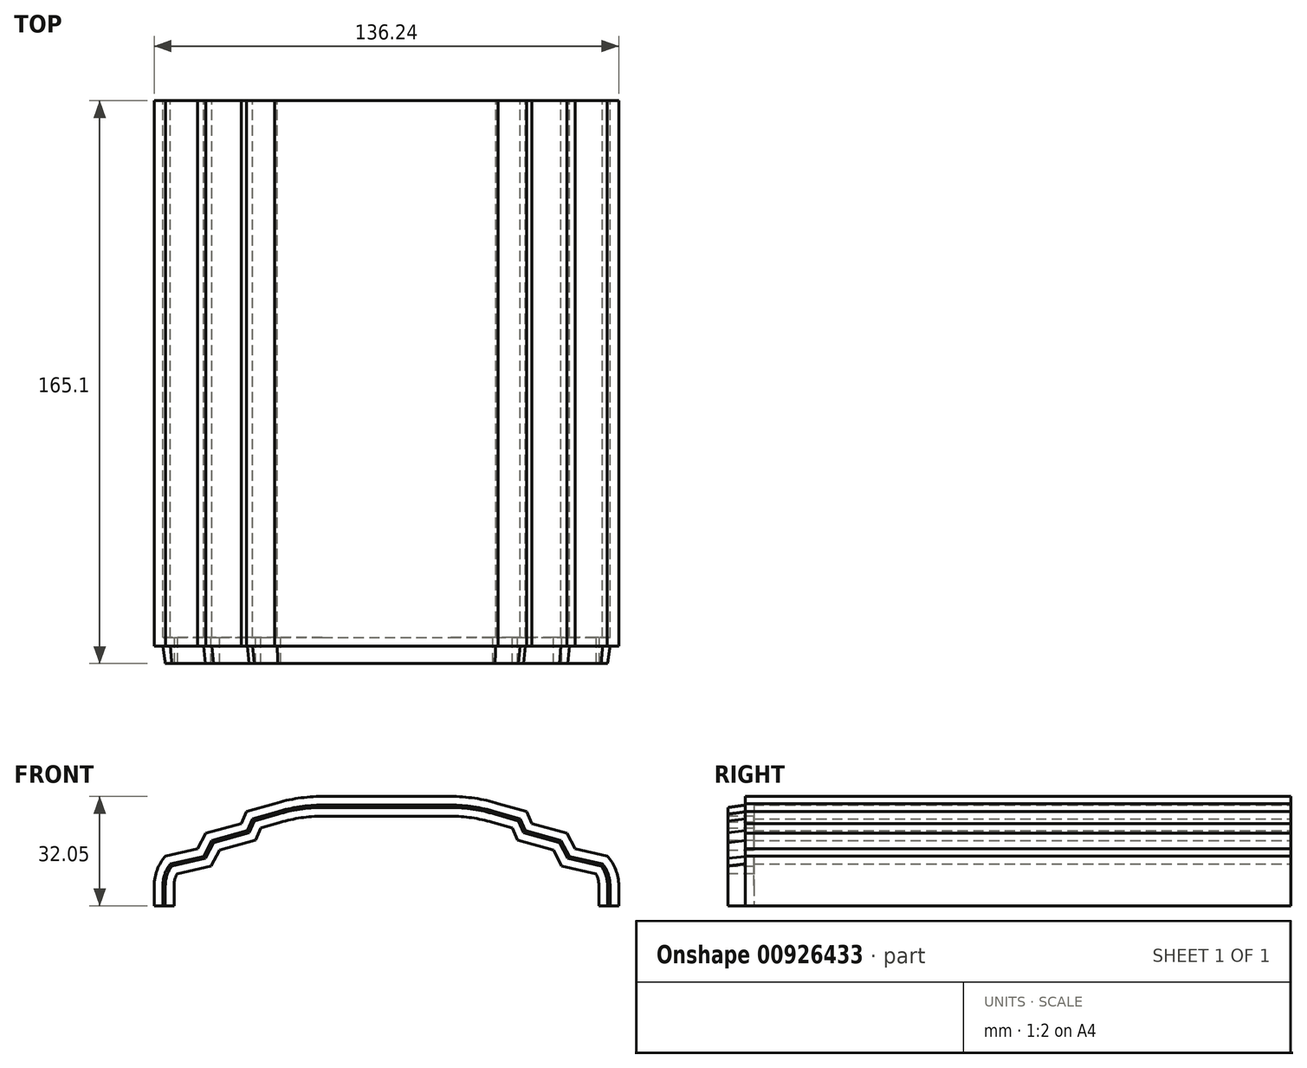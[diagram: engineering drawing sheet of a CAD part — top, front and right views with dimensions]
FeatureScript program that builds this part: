
annotation { "Feature Type Name" : "Feature", "Feature Type Description" : "" }
export const myFeature = defineFeature(function(context is Context, id is Id, definition is map)
    precondition{}
    {
        {
            var Q0;
            Q0=qCreatedBy(makeId("Front.planeOp"),FACE);
            var sketch = newSketch(context, id + "F0", { "sketchPlane" : qUnion([Q0])});
            skLineSegment(sketch, "E0", {"start": v(65.58, 0) * mm, "end": v(68.12, 0) * mm});
            skLineSegment(sketch, "E1", {"start": v(68.12, 0) * mm, "end": v(68.12, 5.92) * mm});
            skArc(sketch, "E2", {"start": v(68.12, 5.92) * mm, "mid": v(67.26, 10.55) * mm, "end": v(64.79, 14.56) * mm});
            skLineSegment(sketch, "E3", {"start": v(64.79, 14.56) * mm, "end": v(55.34, 16.7) * mm});
            skLineSegment(sketch, "E4", {"start": v(55.34, 16.7) * mm, "end": v(52.95, 21.32) * mm});
            skLineSegment(sketch, "E5", {"start": v(52.95, 21.32) * mm, "end": v(42.61, 24.13) * mm});
            skLineSegment(sketch, "E6", {"start": v(42.61, 24.13) * mm, "end": v(41.07, 27.59) * mm});
            skLineSegment(sketch, "E7", {"start": v(41.07, 27.59) * mm, "end": v(32.77, 29.98) * mm});
            skArc(sketch, "E8", {"start": v(32.77, 29.98) * mm, "mid": v(25.87, 31.53) * mm, "end": v(18.83, 32.05) * mm});
            skLineSegment(sketch, "E9", {"start": v(18.83, 32.05) * mm, "end": v(0, 32.05) * mm});
            skLineSegment(sketch, "E10", {"start": v(0, 32.05) * mm, "end": v(0, 29.5) * mm});
            skLineSegment(sketch, "E11.0", {"start": v(18.83, 29.5) * mm, "end": v(0, 29.5) * mm});
            skArc(sketch, "E11.1", {"start": v(32.05, 27.55) * mm, "mid": v(25.51, 29.02) * mm, "end": v(18.83, 29.5) * mm});
            skLineSegment(sketch, "E11.2", {"start": v(39.23, 25.47) * mm, "end": v(32.05, 27.55) * mm});
            skLineSegment(sketch, "E11.3", {"start": v(40.78, 22) * mm, "end": v(39.23, 25.47) * mm});
            skLineSegment(sketch, "E11.4", {"start": v(51.2, 19.16) * mm, "end": v(40.78, 22) * mm});
            skLineSegment(sketch, "E11.5", {"start": v(65.58, 0) * mm, "end": v(65.58, 5.92) * mm});
            skArc(sketch, "E11.6", {"start": v(65.58, 5.92) * mm, "mid": v(65.02, 9.28) * mm, "end": v(63.4, 12.28) * mm});
            skLineSegment(sketch, "E11.7", {"start": v(63.4, 12.28) * mm, "end": v(53.63, 14.49) * mm});
            skLineSegment(sketch, "E11.8", {"start": v(53.63, 14.49) * mm, "end": v(51.2, 19.16) * mm});
            skSolve(sketch);
        }
        {
            var Q0;
            Q0 = qSketchRegion(id + "F0", true);
            extrude(context, id + "F1", {"entities" : qUnion([Q0]), "depth" : 160.02 * mm, "offsetDistance" : 25.4 * mm});
        }
        {
            var Q0;
            Q0=makeQuery(id+"F1.opExtrude","SWEPT_FACE",FACE,{"disambiguationData":[OSD([sQuery(id+"F0.wireOp",EDGE,"E0")])]});
            var sketch = newSketch(context, id + "F2", { "sketchPlane" : qUnion([Q0])});
            skLineSegment(sketch, "E12", {"start": v(62.32, 165.1) * mm, "end": v(64.86, 165.1) * mm});
            skLineSegment(sketch, "E13", {"start": v(64.86, 165.1) * mm, "end": v(65.93, 157.48) * mm});
            skLineSegment(sketch, "E14", {"start": v(65.93, 157.48) * mm, "end": v(62.32, 157.48) * mm});
            skLineSegment(sketch, "E15", {"start": v(62.32, 157.48) * mm, "end": v(62.32, 165.1) * mm});
            skPoint(sketch, "E16", {"position": v(65.58, 160.02) * mm});
            skSolve(sketch);
        }
        {
            var Q0;
            Q0 = qSketchRegion(id + "F2", true);
            var Q1;
            Q1=makeQuery(id+"F1.opExtrude","CAP_EDGE",EDGE,{"disambiguationData":[OSD([sQuery(id+"F0.wireOp",EDGE,"E11.5")])],"isStart":false});
            var Q2;
            Q2=makeQuery(id+"F1.opExtrude","CAP_EDGE",EDGE,{"disambiguationData":[OSD([sQuery(id+"F0.wireOp",EDGE,"E11.6")])],"isStart":false});
            var Q3;
            Q3=makeQuery(id+"F1.opExtrude","CAP_EDGE",EDGE,{"disambiguationData":[OSD([sQuery(id+"F0.wireOp",EDGE,"E11.7")])],"isStart":false});
            var Q4;
            Q4=makeQuery(id+"F1.opExtrude","CAP_EDGE",EDGE,{"disambiguationData":[OSD([sQuery(id+"F0.wireOp",EDGE,"E11.8")])],"isStart":false});
            var Q5;
            Q5=makeQuery(id+"F1.opExtrude","CAP_EDGE",EDGE,{"disambiguationData":[OSD([sQuery(id+"F0.wireOp",EDGE,"E11.4")])],"isStart":false});
            var Q6;
            Q6=makeQuery(id+"F1.opExtrude","CAP_EDGE",EDGE,{"disambiguationData":[OSD([sQuery(id+"F0.wireOp",EDGE,"E11.3")])],"isStart":false});
            var Q7;
            Q7=makeQuery(id+"F1.opExtrude","CAP_EDGE",EDGE,{"disambiguationData":[OSD([sQuery(id+"F0.wireOp",EDGE,"E11.2")])],"isStart":false});
            var Q8;
            Q8=makeQuery(id+"F1.opExtrude","CAP_EDGE",EDGE,{"disambiguationData":[OSD([sQuery(id+"F0.wireOp",EDGE,"E11.1")])],"isStart":false});
            var Q9;
            Q9=makeQuery(id+"F1.opExtrude","CAP_EDGE",EDGE,{"disambiguationData":[OSD([sQuery(id+"F0.wireOp",EDGE,"E11.0")])],"isStart":false});
            sweep(context, id + "F3", {"operationType" : NewBodyOperationType.ADD, "profiles" : qUnion([Q0]), "path" : qUnion([Q1, Q2, Q3, Q4, Q5, Q6, Q7, Q8, Q9])});
        }
        {
            var Q0;
            Q0=makeQuery(id+"F1.opExtrude","SWEPT_BODY",BODY,{"disambiguationData":[OSD([sQuery(id+"F0.wireOp",EDGE,"E0"),sQuery(id+"F0.wireOp",EDGE,"E1"),sQuery(id+"F0.wireOp",EDGE,"E2"),sQuery(id+"F0.wireOp",EDGE,"E3"),sQuery(id+"F0.wireOp",EDGE,"E4"),sQuery(id+"F0.wireOp",EDGE,"E5"),sQuery(id+"F0.wireOp",EDGE,"E6"),sQuery(id+"F0.wireOp",EDGE,"E7"),sQuery(id+"F0.wireOp",EDGE,"E8"),sQuery(id+"F0.wireOp",EDGE,"E9"),sQuery(id+"F0.wireOp",EDGE,"E10"),sQuery(id+"F0.wireOp",EDGE,"E11.0"),sQuery(id+"F0.wireOp",EDGE,"E11.1"),sQuery(id+"F0.wireOp",EDGE,"E11.2"),sQuery(id+"F0.wireOp",EDGE,"E11.3"),sQuery(id+"F0.wireOp",EDGE,"E11.4"),sQuery(id+"F0.wireOp",EDGE,"E11.5"),sQuery(id+"F0.wireOp",EDGE,"E11.6"),sQuery(id+"F0.wireOp",EDGE,"E11.7"),sQuery(id+"F0.wireOp",EDGE,"E11.8")])]});
            var Q1;
            Q1=qCreatedBy(makeId("Right.planeOp"),FACE);
            mirror(context, id + "F4", {"operationType" : NewBodyOperationType.ADD, "entities" : qUnion([Q0]), "mirrorPlane" : qUnion([Q1])});
        }
    });
